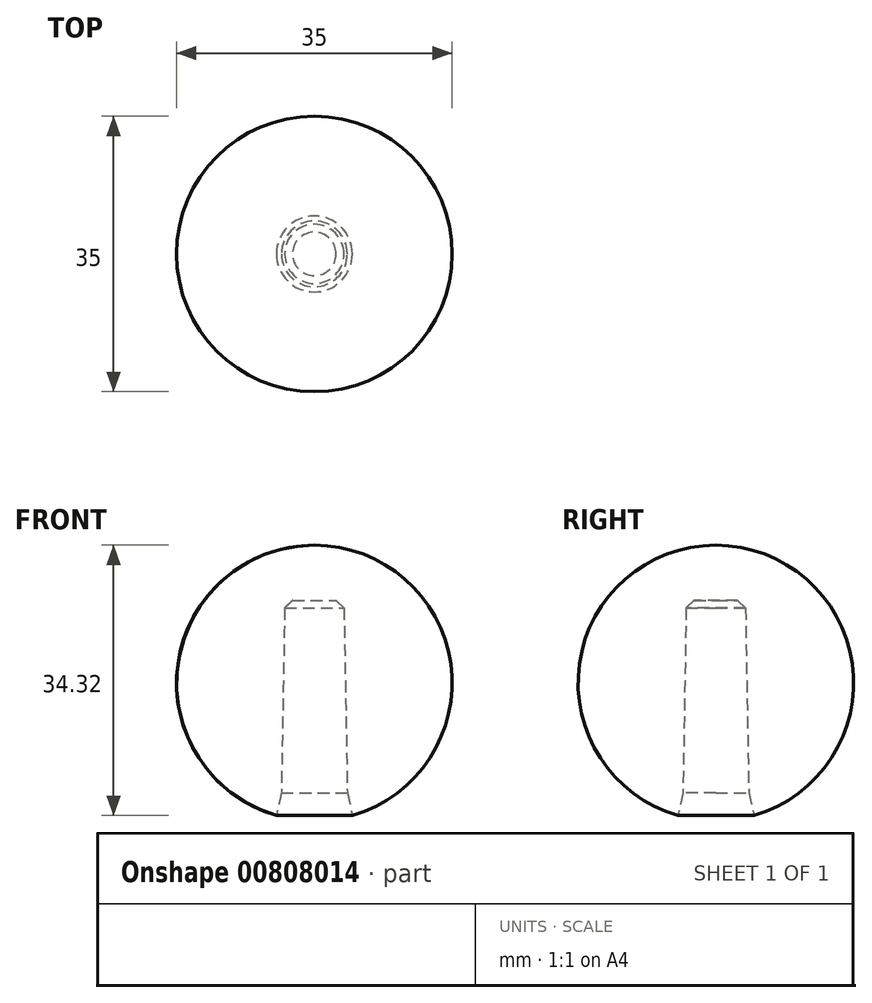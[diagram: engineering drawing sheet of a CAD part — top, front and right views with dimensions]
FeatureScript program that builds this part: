
annotation { "Feature Type Name" : "Feature", "Feature Type Description" : "" }
export const myFeature = defineFeature(function(context is Context, id is Id, definition is map)
    precondition{}
    {
        {
            var Q0;
            Q0=qCreatedBy(makeId("Front.planeOp"),FACE);
            var sketch = newSketch(context, id + "F0", { "sketchPlane" : qUnion([Q0])});
            skArc(sketch, "E0", {"start": v(0, 35) * mm, "mid": v(-17.37, 19.64) * mm, "end": v(-4.24, 0.52) * mm});
            skLineSegment(sketch, "E1", {"start": v(-4.24, 0.52) * mm, "end": v(-3.75, 28) * mm});
            skLineSegment(sketch, "E2", {"start": v(-3.75, 28) * mm, "end": v(0, 28) * mm});
            skPoint(sketch, "E3.orphan", {"position": v(-4.25, 0) * mm});
            skPoint(sketch, "E4.orphan", {"position": v(4.25, 0) * mm});
            skPoint(sketch, "E5.visualSharp", {"position": v(-3.75, 28) * mm});
            skPoint(sketch, "E6.visualSharp", {"position": v(3.75, 28) * mm});
            skPoint(sketch, "E7.visualSharp", {"position": v(2.8, 0.22) * mm});
            skLineSegment(sketch, "E8", {"start": v(0, 54.41) * mm, "end": v(0, -20.98) * mm, "construction": true});
            skLineSegment(sketch, "E9", {"start": v(0, 28) * mm, "end": v(0, 35) * mm});
            skSolve(sketch);
        }
        {
            var Q0;
            Q0=makeQuery(id+"F0.imprint","IMPRINT",FACE,{"disambiguationData":[TD([[makeQuery(id+"F0.imprint","IMPRINT",EDGE,{"derivedFrom":sQuery(id+"F0.wireOp",EDGE,"E0")}),1.0]])]});
            var Q1;
            Q1=sQuery(id+"F0.wireOp",EDGE,"E8");
            revolve(context, id + "F1", {"surfaceOperationType" : NewSurfaceOperationType.NEW, "entities" : qUnion([Q0]), "axis" : qUnion([Q1]), "revolveType" : RevolveType.FULL});
        }
        {
            var Q0;
            Q0=makeQuery(id+"F1.opRevolve","SWEPT_EDGE",EDGE,{"disambiguationData":[OSD([sQuery(id+"F0.wireOp",EDGE,"E0"),sQuery(id+"F0.wireOp",EDGE,"E1")])]});
            chamfer(context, id + "F2", {"entities" : qUnion([Q0]), "chamferType" : ChamferType.TWO_OFFSETS, "width1" : 0.5 * mm, "oppositeDirection" : false, "width2" : 3 * mm, "tangentPropagation" : true});
        }
        {
            var Q0;
            Q0=qCreatedBy(makeId("Top.planeOp"),FACE);
            var sketch = newSketch(context, id + "F3", { "sketchPlane" : qUnion([Q0])});
            skLineSegment(sketch, "E10.bottom", {"start": v(-60.23, 0) * mm, "end": v(63.5, 0) * mm});
            skLineSegment(sketch, "E10.top", {"start": v(-60.23, -50.58) * mm, "end": v(63.5, -50.58) * mm});
            skLineSegment(sketch, "E10.left", {"start": v(-60.23, 0) * mm, "end": v(-60.23, -50.58) * mm});
            skLineSegment(sketch, "E10.right", {"start": v(63.5, 0) * mm, "end": v(63.5, -50.58) * mm});
            skSolve(sketch);
        }
        {
            var Q0;
            Q0=makeQuery(id+"F1.opRevolve","SWEPT_EDGE",EDGE,{"disambiguationData":[OSD([sQuery(id+"F0.wireOp",EDGE,"E1"),sQuery(id+"F0.wireOp",EDGE,"E2")])]});
            chamfer(context, id + "F4", {"entities" : qUnion([Q0]), "width" : 1 * mm, "tangentPropagation" : true});
        }
    });
